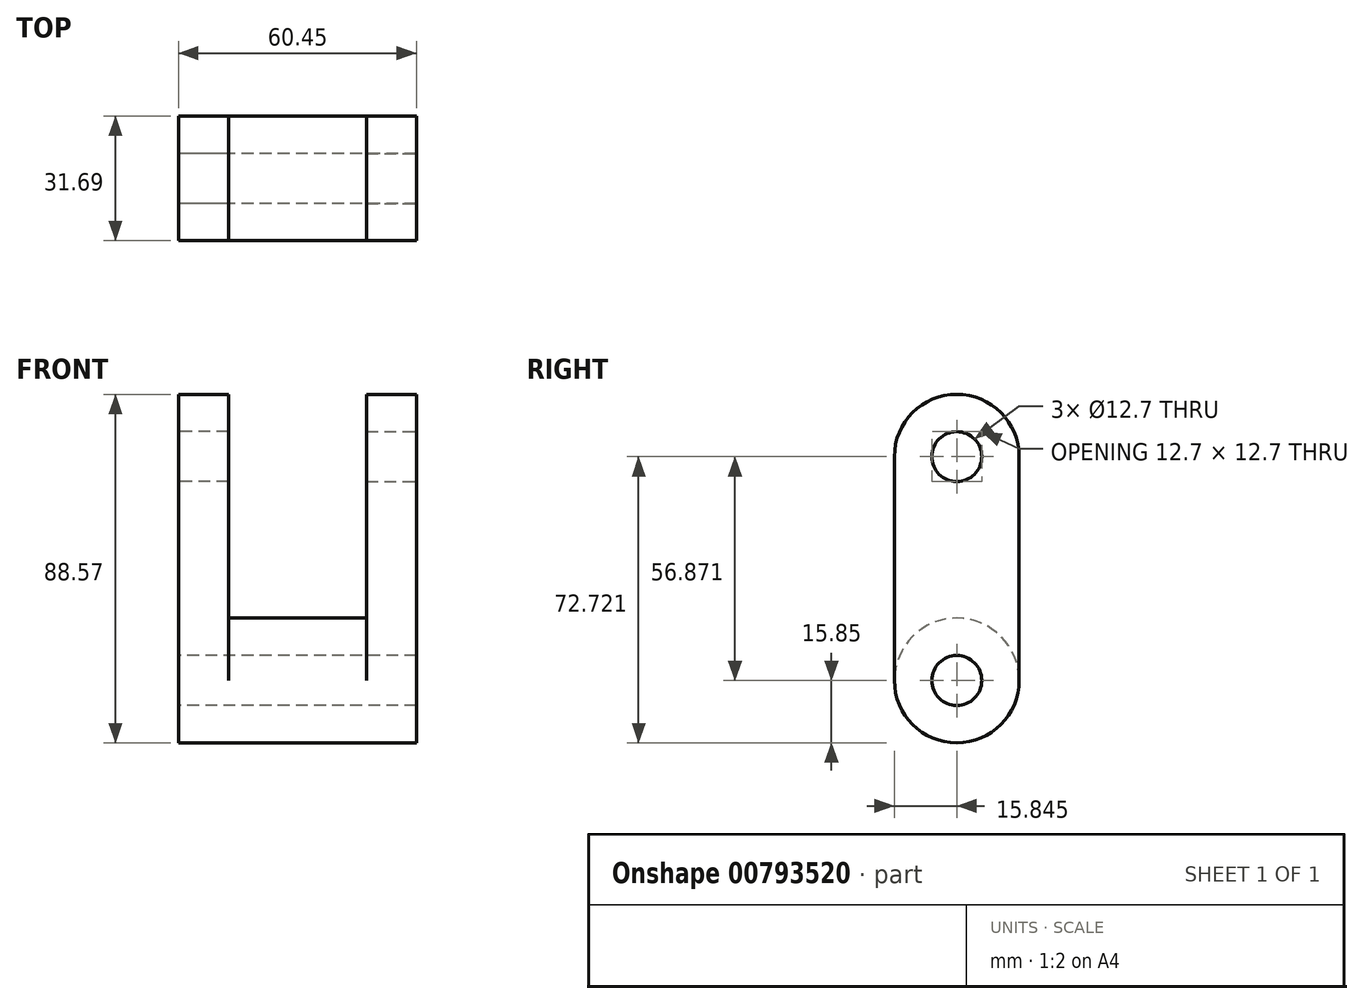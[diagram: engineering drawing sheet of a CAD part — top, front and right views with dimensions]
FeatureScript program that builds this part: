
annotation { "Feature Type Name" : "Feature", "Feature Type Description" : "" }
export const myFeature = defineFeature(function(context is Context, id is Id, definition is map)
    precondition{}
    {
        {
            var Q0;
            Q0=qCreatedBy(makeId("Top.planeOp"),FACE);
            var sketch = newSketch(context, id + "F0", { "sketchPlane" : qUnion([Q0])});
            skLineSegment(sketch, "E0", {"start": v(-55.55, 31.7) * mm, "end": v(-42.85, 31.7) * mm});
            skLineSegment(sketch, "E1", {"start": v(-42.85, 31.7) * mm, "end": v(-42.85, 0) * mm});
            skLineSegment(sketch, "E2", {"start": v(-42.85, 0) * mm, "end": v(-55.55, 0) * mm});
            skLineSegment(sketch, "E3", {"start": v(-55.55, 0) * mm, "end": v(-55.55, 31.7) * mm});
            skSolve(sketch);
        }
        {
            var Q0;
            Q0=makeQuery(id+"F0.imprint","IMPRINT",FACE,{"disambiguationData":[TD([[makeQuery(id+"F0.imprint","IMPRINT",EDGE,{"derivedFrom":sQuery(id+"F0.wireOp",EDGE,"E0")}),-1.0]])]});
            extrude(context, id + "F1", {"entities" : qUnion([Q0]), "depth" : 76.2 * mm, "offsetDistance" : 25.4 * mm});
        }
        {
            var Q0;
            Q0=makeQuery(id+"F1.opExtrude","SWEPT_FACE",FACE,{"disambiguationData":[OSD([sQuery(id+"F0.wireOp",EDGE,"E3")])]});
            var sketch = newSketch(context, id + "F2", { "sketchPlane" : qUnion([Q0])});
            skCircle(sketch, "E4", {"center": v(-15.85, 0) * mm, "radius": 15.85 * mm});
            skCircle(sketch, "E5", {"center": v(-15.85, 0) * mm, "radius": 6.35 * mm});
            skArc(sketch, "E6", {"start": v(0, 56.87) * mm, "mid": v(-15.85, 72.72) * mm, "end": v(-31.7, 56.87) * mm});
            skCircle(sketch, "E7", {"center": v(-15.85, 56.87) * mm, "radius": 6.35 * mm});
            skSolve(sketch);
        }
        {
            var Q0;
            {var subQ1=sQuery(id+"F0.wireOp",EDGE,"E3");var subQ2=makeQuery(id+"F1.opExtrude","CAP_EDGE",EDGE,{"disambiguationData":[OSD([subQ1])],"isStart":true});var subQ5=sQuery(id+"F2.wireOp",EDGE,"E5");var subQ6=makeQuery(id+"F2.imprint","INTERSECT",VERTEX,{"disambiguationData":[OD(0.0)],"derivedFrom":[subQ2,subQ5]});Q0=makeQuery(id+"F2.imprint","IMPRINT",FACE,{"disambiguationData":[TD([[makeQuery(id+"F2.imprint","IMPRINT",EDGE,{"disambiguationData":[TD([[subQ6,1.0]])],"derivedFrom":subQ5}),-1.0]])]});}
            var Q1;
            {var subQ1=sQuery(id+"F0.wireOp",EDGE,"E3");var subQ2=makeQuery(id+"F1.opExtrude","CAP_EDGE",EDGE,{"disambiguationData":[OSD([subQ1])],"isStart":true});var subQ5=sQuery(id+"F2.wireOp",EDGE,"E5");var subQ6=makeQuery(id+"F2.imprint","INTERSECT",VERTEX,{"disambiguationData":[OD(0.0)],"derivedFrom":[subQ2,subQ5]});Q1=makeQuery(id+"F2.imprint","IMPRINT",FACE,{"disambiguationData":[TD([[makeQuery(id+"F2.imprint","IMPRINT",EDGE,{"disambiguationData":[TD([[subQ6,-1.0]])],"derivedFrom":subQ5}),-1.0]])]});}
            extrude(context, id + "F3", {"entities" : qUnion([Q0, Q1]), "operationType" : NewBodyOperationType.ADD, "oppositeDirection" : true, "depth" : 30.23 * mm, "offsetDistance" : 25.4 * mm});
        }
        {
            var Q0;
            {var subQ0=sQuery(id+"F2.wireOp",EDGE,"E5");var subQ1=makeQuery(id+"F1.opExtrude","CAP_EDGE",EDGE,{"disambiguationData":[OSD([sQuery(id+"F0.wireOp",EDGE,"E3")])],"isStart":true});var subQ2=makeQuery(id+"F2.imprint","INTERSECT",VERTEX,{"disambiguationData":[OD(0.0)],"derivedFrom":[subQ1,subQ0]});Q0=makeQuery(id+"F2.imprint","IMPRINT",FACE,{"disambiguationData":[TD([[makeQuery(id+"F2.imprint","IMPRINT",EDGE,{"disambiguationData":[TD([[subQ2,1.0]])],"derivedFrom":subQ0}),1.0]])]});}
            extrude(context, id + "F4", {"entities" : qUnion([Q0]), "operationType" : NewBodyOperationType.REMOVE, "oppositeDirection" : true, "depth" : 25.4 * mm, "offsetDistance" : 25.4 * mm});
        }
        {
            var Q0;
            {var subQ0=sQuery(id+"F2.wireOp",EDGE,"E6");Q0=makeQuery(id+"F2.imprint","IMPRINT",FACE,{"disambiguationData":[TD([[makeQuery(id+"F2.imprint","IMPRINT",EDGE,{"derivedFrom":subQ0}),-1.0]])]});}
            extrude(context, id + "F5", {"entities" : qUnion([Q0]), "operationType" : NewBodyOperationType.REMOVE, "oppositeDirection" : true, "depth" : 25.4 * mm, "offsetDistance" : 25.4 * mm});
        }
        {
            var Q0;
            Q0=makeQuery(id+"F2.imprint","IMPRINT",FACE,{"disambiguationData":[TD([[makeQuery(id+"F2.imprint","IMPRINT",EDGE,{"derivedFrom":sQuery(id+"F2.wireOp",EDGE,"E7")}),1.0]])]});
            extrude(context, id + "F6", {"entities" : qUnion([Q0]), "operationType" : NewBodyOperationType.REMOVE, "oppositeDirection" : true, "depth" : 25.4 * mm, "offsetDistance" : 25.4 * mm});
        }
        {
            var Q0;
            Q0=makeQuery(id+"F1.opExtrude","SWEPT_BODY",BODY,{"disambiguationData":[OSD([sQuery(id+"F0.wireOp",EDGE,"E0"),sQuery(id+"F0.wireOp",EDGE,"E1"),sQuery(id+"F0.wireOp",EDGE,"E2"),sQuery(id+"F0.wireOp",EDGE,"E3")])]});
            var Q1;
            Q1=makeQuery(id+"F3.opExtrude","CAP_FACE",FACE,{"disambiguationData":[OSD([sQuery(id+"F2.wireOp",EDGE,"E4"),sQuery(id+"F2.wireOp",EDGE,"E5")])],"isStart":false});
            mirror(context, id + "F7", {"operationType" : NewBodyOperationType.ADD, "entities" : qUnion([Q0]), "mirrorPlane" : qUnion([Q1])});
        }
    });
